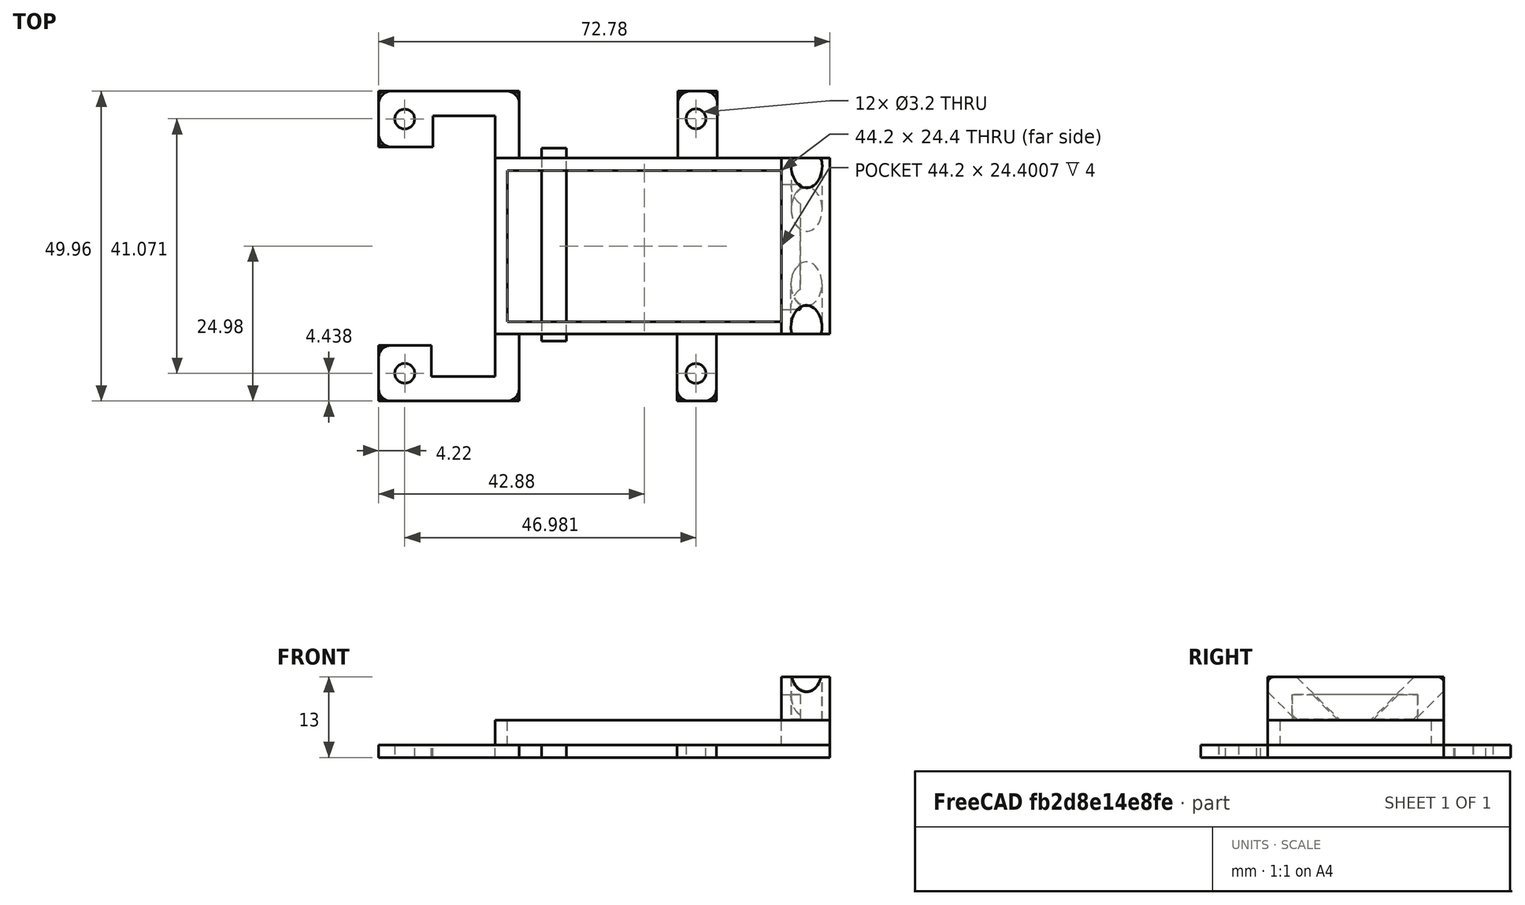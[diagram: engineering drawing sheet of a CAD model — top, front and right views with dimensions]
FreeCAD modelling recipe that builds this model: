
FCSTD DOCUMENT  (FreeCAD 0.16R6703 (Git))
Label: Receiver Support
License: FreeArt
LicenseURL: http://artlibre.org/licence/lal
objects: Sketcher::SketchObject×7, PartDesign::Pad×5, PartDesign::Fillet×3, Part::Cut×2, PartDesign::Pocket×2, Mesh::Feature×1, Part::Fuse×1
note: 27 computed .brp shape members not serialized (recipe doc carries the construction recipe); baked Part::Feature solids carry a one-line shape summary decoded from their .brp

FEATURE [Mesh::Feature] Spacer_Botton_10mm  label="Spacer-Botton 10mm"
FEATURE [Sketcher::SketchObject] Sketch
  sketch-geometry (28):
    g0: LineSegment StartX=21.7667 StartY=-25.4923 StartZ=0 EndX=21.7667 EndY=-16.5308 EndZ=0
    g1: LineSegment StartX=21.7667 StartY=-16.5308 StartZ=0 EndX=30.2907 EndY=-16.5308 EndZ=0
    g2: LineSegment StartX=30.2907 StartY=-16.5308 StartZ=0 EndX=30.2907 EndY=-21.5278 EndZ=0
    g3: LineSegment StartX=30.2907 StartY=-21.5278 StartZ=0 EndX=40.5459 EndY=-21.5278 EndZ=0
    g4: LineSegment StartX=40.5459 StartY=-21.5278 StartZ=0 EndX=40.5459 EndY=20.4801 EndZ=0
    g5: LineSegment StartX=21.7928 StartY=15.4956 StartZ=0 EndX=21.7928 EndY=24.4708 EndZ=0
    g6: LineSegment StartX=76.4105 StartY=24.4708 StartZ=0 EndX=76.4105 EndY=13.6892 EndZ=0
    g7: LineSegment StartX=76.4105 StartY=13.6892 StartZ=0 EndX=94.5459 EndY=13.6892 EndZ=0
    g8: LineSegment StartX=94.5459 StartY=13.6892 StartZ=0 EndX=94.5459 EndY=-14.7108 EndZ=0
    g9: LineSegment StartX=94.5459 StartY=-14.7108 StartZ=0 EndX=76.2605 EndY=-14.7108 EndZ=0
    g10: LineSegment StartX=76.2605 StartY=-14.7108 StartZ=0 EndX=76.2605 EndY=-25.4923 EndZ=0
    g11: LineSegment StartX=21.7928 StartY=15.4956 StartZ=0 EndX=30.5459 EndY=15.4956 EndZ=0
    g12: LineSegment StartX=30.5459 StartY=15.4956 StartZ=0 EndX=30.5459 EndY=20.4801 EndZ=0
    g13: LineSegment StartX=30.5459 StartY=20.4801 StartZ=0 EndX=40.5459 EndY=20.4801 EndZ=0
    g14: LineSegment StartX=21.7667 StartY=-25.4923 StartZ=0 EndX=44.438 EndY=-25.4923 EndZ=0
    g15: LineSegment StartX=44.438 StartY=-25.4923 StartZ=0 EndX=44.438 EndY=-14.7108 EndZ=0
    g16: LineSegment StartX=44.438 StartY=-14.7108 StartZ=0 EndX=69.874 EndY=-14.7108 EndZ=0
    g17: LineSegment StartX=69.874 StartY=-14.7108 StartZ=0 EndX=69.874 EndY=-25.4923 EndZ=0
    g18: LineSegment StartX=69.874 StartY=-25.4923 StartZ=0 EndX=76.2605 EndY=-25.4923 EndZ=0
    g19: LineSegment StartX=21.7928 StartY=24.4708 StartZ=0 EndX=44.4641 EndY=24.4708 EndZ=0
    g20: LineSegment StartX=44.4641 StartY=24.4708 StartZ=0 EndX=44.4641 EndY=13.6892 EndZ=0
    g21: LineSegment StartX=44.4641 StartY=13.6892 StartZ=0 EndX=70.024 EndY=13.6892 EndZ=0
    g22: LineSegment StartX=70.024 StartY=13.6892 StartZ=0 EndX=70.024 EndY=24.4708 EndZ=0
    g23: LineSegment StartX=70.024 StartY=24.4708 StartZ=0 EndX=76.4105 EndY=24.4708 EndZ=0
    g24: Circle CenterX=25.9899 CenterY=19.9708 CenterZ=0 NormalX=0 NormalY=0 NormalZ=1 Radius=1.6
    g25: Circle CenterX=25.9984 CenterY=-21.0187 CenterZ=0 NormalX=0 NormalY=0 NormalZ=1 Radius=1.6
    g26: Circle CenterX=72.9705 CenterY=20.0188 CenterZ=0 NormalX=0 NormalY=0 NormalZ=1 Radius=1.6
    g27: Circle CenterX=72.9475 CenterY=-21.0524 CenterZ=0 NormalX=0 NormalY=0 NormalZ=1 Radius=1.6
  constraints (84):
    c: Vertical(g0)
    c: Coincident(g0,g1)
    c: Horizontal(g1)
    c: Coincident(g1,g2)
    c: Coincident(g2,g3)
    c: Horizontal(g3)
    c: Coincident(g3,g4)
    c: Vertical(g4)
    c: Vertical(g5)
    c: Vertical(g6)
    c: Coincident(g6,g7)
    c: Horizontal(g7)
    c: Coincident(g7,g8)
    c: Vertical(g8)
    c: Coincident(g8,g9)
    c: Horizontal(g9)
    c: Coincident(g9,g10)
    c: Vertical(g10)
    c: Horizontal(g11)
    c: Coincident(g11,g12)
    c: Vertical(g12)
    c: Coincident(g12,g13)
    c: Horizontal(g13)
    c: Coincident(g4,g13)
    c: DistanceY(g-1,g5) = 24.4708
    c: Coincident(g11,g5)
    c: DistanceX(g-2,g5) = 21.7928
    c: Distance(g11) = 8.75309
    c: DistanceY(g12,g12) = 4.98454
    c: DistanceY(g5,g5) = 8.97522
    c: DistanceX(g-2,g0) = 21.7667
    c: DistanceY(g-1,g0) = -25.4923
    c: Vertical(g2)
    c: DistanceY(g0,g0) = 8.96148
    c: DistanceX(g1,g1) = 8.52402
    c: DistanceY(g2,g2) = 4.99701
    c: Equal(g10,g6)
    c: DistanceX(g5,g6) = 54.6177
    c: DistanceX(g13,g13) = 10
    c: Distance(g8,g4) = 54
    c: Coincident(g0,g14)
    c: Horizontal(g14)
    c: Coincident(g14,g15)
    c: Vertical(g15)
    c: Coincident(g15,g16)
    c: Horizontal(g16)
    c: Coincident(g16,g17)
    c: Vertical(g17)
    c: Coincident(g17,g18)
    c: Coincident(g18,g10)
    c: Horizontal(g18)
    c: Coincident(g5,g19)
    c: Horizontal(g19)
    c: Coincident(g19,g20)
    c: Vertical(g20)
    c: Coincident(g20,g21)
    c: Horizontal(g21)
    c: Coincident(g21,g22)
    c: Vertical(g22)
    c: Coincident(g22,g23)
    c: Coincident(g23,g6)
    c: Horizontal(g23)
    c: Radius(g24) = 1.6
    c: Distance(g24,g19) = 4.5
    c: Distance(g24,g12) = 4.55598
    c: Radius(g25) = 1.6
    c: Distance(g25,g0) = 4.23168
    c: Distance(g25,g14) = 4.47363
    c: Distance(g20,g12) = 13.9182
    c: Equal(g19,g14)
    c: Distance(g20,g16) = 28.4
    c: Equal(g15,g20)
    c: Equal(g22,g20)
    c: Equal(g20,g17)
    c: Equal(g10,g17)
    c: DistanceX(g18,g18) = 6.38646
    c: Equal(g23,g18)
    c: DistanceX(g16,g16) = 25.436
    c: Radius(g26) = 1.6
    c: Distance(g26,g23) = 4.45203
    c: Distance(g26,g22) = 2.9465
    c: Radius(g27) = 1.6
    c: Distance(g27,g18) = 4.43991
    c: Distance(g27,g17) = 3.07355
FEATURE [PartDesign::Pad] Pad
  Length = 2
  Length2 = 100
  Sketch = -> Sketch
  Type = 0
FEATURE [Sketcher::SketchObject] Sketch001
  Placement = pos=(0,0,2) rot=(0,0,1;0rad)
  Support = -> Pad [Face30]
  sketch-geometry (8):
    g0: LineSegment StartX=40.5505 StartY=13.6902 StartZ=0 EndX=94.5451 EndY=13.6902 EndZ=0
    g1: LineSegment StartX=94.5451 StartY=13.6902 StartZ=0 EndX=94.5451 EndY=-14.7105 EndZ=0
    g2: LineSegment StartX=94.5451 StartY=-14.7105 StartZ=0 EndX=40.5505 EndY=-14.7105 EndZ=0
    g3: LineSegment StartX=40.5505 StartY=-14.7105 StartZ=0 EndX=40.5505 EndY=13.6902 EndZ=0
    g4: LineSegment StartX=42.5505 StartY=11.6902 StartZ=0 EndX=86.7505 EndY=11.6902 EndZ=0
    g5: LineSegment StartX=86.7505 StartY=11.6902 StartZ=0 EndX=86.7505 EndY=-12.7105 EndZ=0
    g6: LineSegment StartX=86.7505 StartY=-12.7105 StartZ=0 EndX=42.5505 EndY=-12.7105 EndZ=0
    g7: LineSegment StartX=42.5505 StartY=-12.7105 StartZ=0 EndX=42.5505 EndY=11.6902 EndZ=0
  constraints (24):
    c: Coincident(g0,g1)
    c: Coincident(g1,g2)
    c: Coincident(g2,g3)
    c: Coincident(g3,g0)
    c: Horizontal(g0)
    c: Horizontal(g2)
    c: Vertical(g1)
    c: Vertical(g3)
    c: Distance(g-1,g3) = 40.5505
    c: DistanceY(g-1,g0) = 13.6902
    c: DistanceX(g-2,g1) = 94.5451
    c: DistanceY(g-1,g2) = -14.7105
    c: Coincident(g4,g5)
    c: Coincident(g5,g6)
    c: Coincident(g6,g7)
    c: Coincident(g7,g4)
    c: Horizontal(g4)
    c: Horizontal(g6)
    c: Vertical(g5)
    c: Vertical(g7)
    c: Distance(g6,g3) = 2
    c: Distance(g6,g2) = 2
    c: Distance(g4,g0) = 2
    c: DistanceX(g4,g4) = 44.2
FEATURE [PartDesign::Pad] Pad001
  Length = 4
  Length2 = 100
  Sketch = -> Sketch001
  Type = 0
FEATURE [PartDesign::Fillet] Fillet
  Base = -> Pad001 [Edge2,Edge1,Edge5,Edge86,Edge85,Edge76,Edge74,Edge68,Edge67,Edge66]
  Radius = 2
FEATURE [Sketcher::SketchObject] Sketch002
  Placement = pos=(0.5,-2,16) rot=(1,0,0;0.785398rad)
  sketch-geometry (1):
    g0: Circle CenterX=90.269 CenterY=-10.3263 CenterZ=0 NormalX=0 NormalY=0 NormalZ=1 Radius=2.5
  constraints (1):
    c: Radius(g0) = 2.5
FEATURE [PartDesign::Pad] Pad002
  Length = 15
  Length2 = 100
  Midplane = true
  Placement = pos=(0.5,-2,16) rot=(1,0,0;0.785398rad)
  Sketch = -> Sketch002
  Type = 0
FEATURE [Sketcher::SketchObject] Sketch004
  Placement = pos=(0,0,6) rot=(0,0,1;0rad)
  sketch-geometry (4):
    g0: LineSegment StartX=86.7531 StartY=13.6881 StartZ=0 EndX=94.5459 EndY=13.6881 EndZ=0
    g1: LineSegment StartX=94.5459 StartY=13.6881 StartZ=0 EndX=94.5459 EndY=-14.7104 EndZ=0
    g2: LineSegment StartX=94.5459 StartY=-14.7104 StartZ=0 EndX=86.7531 EndY=-14.7104 EndZ=0
    g3: LineSegment StartX=86.7531 StartY=-14.7104 StartZ=0 EndX=86.7531 EndY=13.6881 EndZ=0
  constraints (12):
    c: Coincident(g0,g1)
    c: Coincident(g1,g2)
    c: Coincident(g2,g3)
    c: Coincident(g3,g0)
    c: Horizontal(g0)
    c: Horizontal(g2)
    c: Vertical(g1)
    c: Vertical(g3)
    c: DistanceY(g-1,g0) = 13.6881
    c: DistanceX(g-2,g0) = 86.7531
    c: DistanceX(g0,g0) = 7.7928
    c: DistanceY(g-1,g2) = -14.7104
FEATURE [PartDesign::Pad] Pad004
  Length = 7
  Length2 = 100
  Placement = pos=(0,0,6) rot=(0,0,1;0rad)
  Sketch = -> Sketch004
  Type = 0
FEATURE [Sketcher::SketchObject] Sketch003
  Placement = pos=(0,8,9) rot=(-1,0,0;0.785398rad)
  sketch-geometry (1):
    g0: Circle CenterX=90.8091 CenterY=0.294413 CenterZ=0 NormalX=0 NormalY=0 NormalZ=1 Radius=2.5
  constraints (1):
    c: Radius(g0) = 2.5
FEATURE [PartDesign::Pad] Pad003
  Length = 14.5
  Length2 = 100
  Midplane = true
  Placement = pos=(0,8,9) rot=(-1,0,0;0.785398rad)
  Sketch = -> Sketch003
  Type = 0
FEATURE [Part::Cut] Cut
  Base = -> Pad004
  Tool = -> Pad003
FEATURE [Part::Cut] Cut001
  Base = -> Cut
  Tool = -> Pad002
FEATURE [Sketcher::SketchObject] Sketch006
  Placement = pos=(86.7531,0,0) rot=(0.57735,-0.57735,-0.57735;2.0944rad)
  Support = -> Cut001 [Face6]
  sketch-geometry (4):
    g0: LineSegment StartX=-9.46073 StartY=10.1216 StartZ=0 EndX=10.7572 EndY=10.1216 EndZ=0
    g1: LineSegment StartX=10.7572 StartY=10.1216 StartZ=0 EndX=10.7572 EndY=6.12159 EndZ=0
    g2: LineSegment StartX=10.7572 StartY=6.12159 StartZ=0 EndX=-9.46073 EndY=6.12159 EndZ=0
    g3: LineSegment StartX=-9.46073 StartY=6.12159 StartZ=0 EndX=-9.46073 EndY=10.1216 EndZ=0
  constraints (9):
    c: Coincident(g0,g1)
    c: Coincident(g1,g2)
    c: Coincident(g2,g3)
    c: Coincident(g3,g0)
    c: Horizontal(g0)
    c: Horizontal(g2)
    c: Vertical(g1)
    c: Vertical(g3)
    c: DistanceY(g3,g3) = 4
FEATURE [PartDesign::Pocket] Pocket
  Length = 3
  Sketch = -> Sketch006
  Type = 0
FEATURE [Part::Fuse] Fusion
  Base = -> Pad001
  Tool = -> Pocket
FEATURE [PartDesign::Fillet] Fillet001
  Base = -> Fusion [Edge131,Edge129,Edge121,Edge118]
  Radius = 1
FEATURE [PartDesign::Fillet] Fillet002
  Base = -> Fillet001 [Edge155,Edge157,Edge163,Edge125,Edge140,Edge126,Edge142,Edge174,Edge176,Edge144]
  Radius = 1
FEATURE [Sketcher::SketchObject] Sketch007
  Placement = pos=(0,0,0) rot=(1,0,0;3.14159rad)
  Support = -> Fillet002 [Face37]
  sketch-geometry (4):
    g0: LineSegment StartX=48.0462 StartY=15.8495 StartZ=0 EndX=52.0462 EndY=15.8495 EndZ=0
    g1: LineSegment StartX=52.0462 StartY=15.8495 StartZ=0 EndX=52.0462 EndY=-15.3015 EndZ=0
    g2: LineSegment StartX=52.0462 StartY=-15.3015 StartZ=0 EndX=48.0462 EndY=-15.3015 EndZ=0
    g3: LineSegment StartX=48.0462 StartY=-15.3015 StartZ=0 EndX=48.0462 EndY=15.8495 EndZ=0
  constraints (9):
    c: Coincident(g0,g1)
    c: Coincident(g1,g2)
    c: Coincident(g2,g3)
    c: Coincident(g3,g0)
    c: Horizontal(g0)
    c: Horizontal(g2)
    c: Vertical(g1)
    c: Vertical(g3)
    c: DistanceX(g2,g2) = 4
FEATURE [PartDesign::Pocket] Pocket001
  Length = 2
  Sketch = -> Sketch007
  Type = 0
